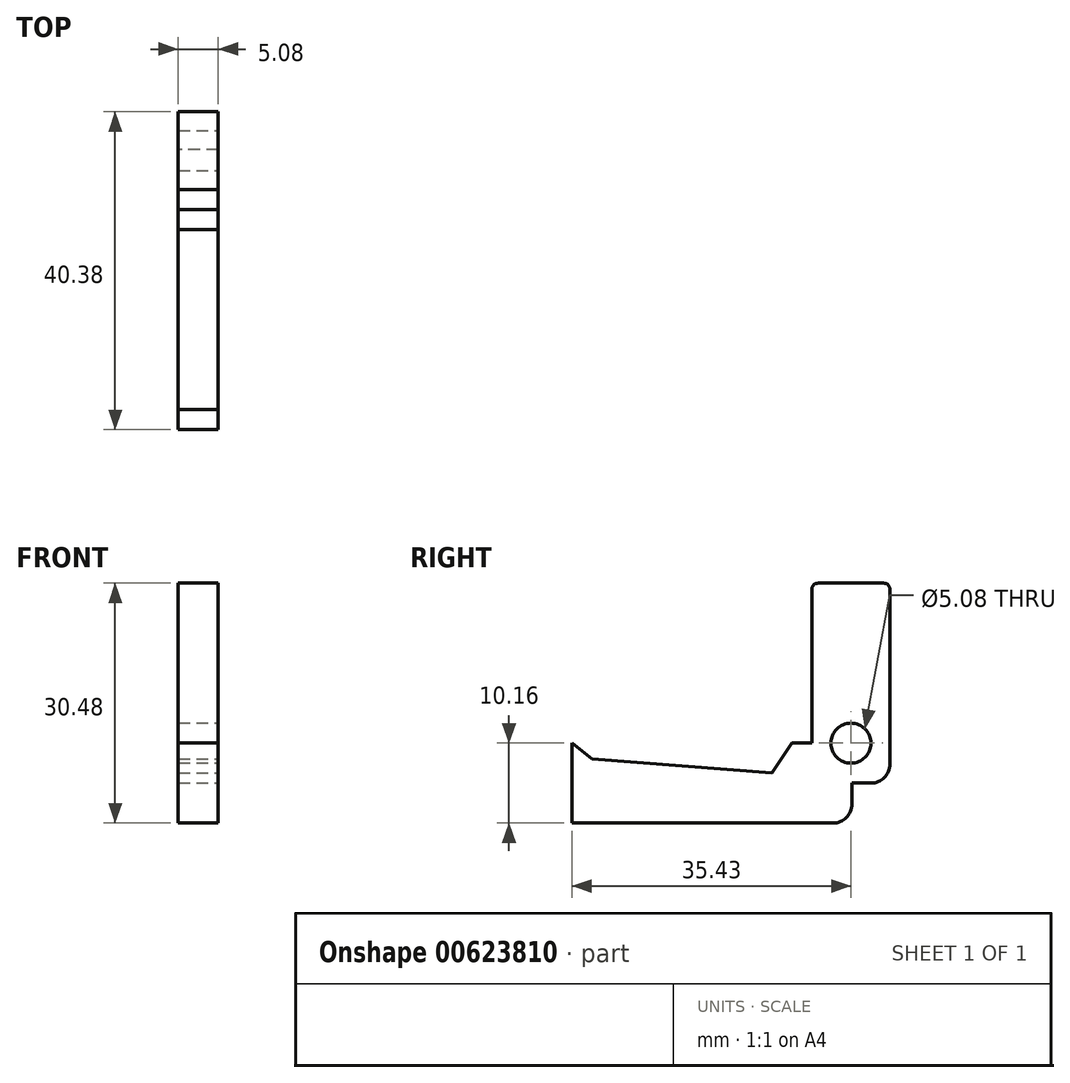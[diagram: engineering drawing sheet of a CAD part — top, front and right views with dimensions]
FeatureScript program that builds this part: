
annotation { "Feature Type Name" : "Feature", "Feature Type Description" : "" }
export const myFeature = defineFeature(function(context is Context, id is Id, definition is map)
    precondition{}
    {
        {
            var Q0;
            Q0=qCreatedBy(makeId("Top.planeOp"),FACE);
            var sketch = newSketch(context, id + "F0", { "sketchPlane" : qUnion([Q0])});
            skLineSegment(sketch, "E0.bottom", {"start": v(-2.54, 4.95) * mm, "end": v(2.54, 4.95) * mm});
            skLineSegment(sketch, "E0.top", {"start": v(-2.54, -4.95) * mm, "end": v(2.54, -4.95) * mm});
            skLineSegment(sketch, "E0.left", {"start": v(-2.54, 4.95) * mm, "end": v(-2.54, -4.95) * mm});
            skLineSegment(sketch, "E0.right", {"start": v(2.54, 4.95) * mm, "end": v(2.54, -4.95) * mm});
            skPoint(sketch, "E0.middle", {"position": v(0, 0) * mm});
            skSolve(sketch);
        }
        {
            var Q0;
            Q0=makeQuery(id+"F0.imprint","IMPRINT",FACE,{"disambiguationData":[TD([[makeQuery(id+"F0.imprint","IMPRINT",EDGE,{"derivedFrom":sQuery(id+"F0.wireOp",EDGE,"E0.bottom")}),-1.0]])]});
            extrude(context, id + "F1", {"entities" : qUnion([Q0]), "depth" : 25.4 * mm, "offsetDistance" : 25.4 * mm});
        }
        {
            var Q0;
            Q0=makeQuery(id+"F1.opExtrude","SWEPT_FACE",FACE,{"disambiguationData":[OSD([sQuery(id+"F0.wireOp",EDGE,"E0.top")])]});
            var sketch = newSketch(context, id + "F2", { "sketchPlane" : qUnion([Q0])});
            skLineSegment(sketch, "E1.bottom", {"start": v(2.54, 0) * mm, "end": v(-2.54, 0) * mm});
            skLineSegment(sketch, "E1.top", {"start": v(2.54, 5.08) * mm, "end": v(-2.54, 5.08) * mm});
            skLineSegment(sketch, "E1.left", {"start": v(2.54, 0) * mm, "end": v(2.54, 5.08) * mm});
            skLineSegment(sketch, "E1.right", {"start": v(-2.54, 0) * mm, "end": v(-2.54, 5.08) * mm});
            skSolve(sketch);
        }
        {
            var Q0;
            Q0=makeQuery(id+"F2.imprint","IMPRINT",FACE,{"disambiguationData":[TD([[makeQuery(id+"F2.imprint","IMPRINT",EDGE,{"derivedFrom":sQuery(id+"F2.wireOp",EDGE,"E1.bottom")}),1.0]])]});
            extrude(context, id + "F3", {"entities" : qUnion([Q0]), "operationType" : NewBodyOperationType.ADD, "depth" : 5.08 * mm, "offsetDistance" : 25.4 * mm});
        }
        {
            var Q0;
            Q0=makeQuery(id+"F3.boolean.opBoolean","MERGE",FACE,{"derivedFrom":[makeQuery(id+"F1.opExtrude","CAP_FACE",FACE,{"disambiguationData":[OSD([sQuery(id+"F0.wireOp",EDGE,"E0.bottom"),sQuery(id+"F0.wireOp",EDGE,"E0.top"),sQuery(id+"F0.wireOp",EDGE,"E0.left"),sQuery(id+"F0.wireOp",EDGE,"E0.right")])],"isStart":true}),makeQuery(id+"F3.opExtrude","SWEPT_FACE",FACE,{"disambiguationData":[OSD([sQuery(id+"F2.wireOp",EDGE,"E1.bottom")])]})]});
            var sketch = newSketch(context, id + "F4", { "sketchPlane" : qUnion([Q0])});
            skLineSegment(sketch, "E2.bottom", {"start": v(2.54, 10.03) * mm, "end": v(-2.54, 10.03) * mm});
            skLineSegment(sketch, "E2.top", {"start": v(2.54, 4.95) * mm, "end": v(-2.54, 4.95) * mm});
            skLineSegment(sketch, "E2.left", {"start": v(2.54, 10.03) * mm, "end": v(2.54, 4.95) * mm});
            skLineSegment(sketch, "E2.right", {"start": v(-2.54, 10.03) * mm, "end": v(-2.54, 4.95) * mm});
            skSolve(sketch);
        }
        {
            var Q0;
            Q0=makeQuery(id+"F4.imprint","IMPRINT",FACE,{"disambiguationData":[TD([[makeQuery(id+"F4.imprint","IMPRINT",EDGE,{"derivedFrom":sQuery(id+"F4.wireOp",EDGE,"E2.bottom")}),-1.0]])]});
            extrude(context, id + "F5", {"entities" : qUnion([Q0]), "operationType" : NewBodyOperationType.ADD, "depth" : 5.08 * mm, "offsetDistance" : 25.4 * mm});
        }
        {
            var Q0;
            Q0=makeQuery(id+"F5.opExtrude","SWEPT_FACE",FACE,{"disambiguationData":[OSD([sQuery(id+"F4.wireOp",EDGE,"E2.top")])]});
            extrude(context, id + "F6", {"entities" : qUnion([Q0]), "operationType" : NewBodyOperationType.ADD, "depth" : 5.08 * mm, "offsetDistance" : 25.4 * mm});
        }
        {
            var Q0;
            Q0=makeQuery(id+"F5.boolean.opBoolean","MERGE",FACE,{"derivedFrom":[makeQuery(id+"F3.opExtrude","CAP_FACE",FACE,{"disambiguationData":[OSD([sQuery(id+"F2.wireOp",EDGE,"E1.bottom"),sQuery(id+"F2.wireOp",EDGE,"E1.top"),sQuery(id+"F2.wireOp",EDGE,"E1.left"),sQuery(id+"F2.wireOp",EDGE,"E1.right")])],"isStart":false}),makeQuery(id+"F5.opExtrude","SWEPT_FACE",FACE,{"disambiguationData":[OSD([sQuery(id+"F4.wireOp",EDGE,"E2.bottom")])]})]});
            extrude(context, id + "F7", {"entities" : qUnion([Q0]), "operationType" : NewBodyOperationType.ADD, "depth" : 25.4 * mm, "offsetDistance" : 25.4 * mm});
        }
        {
            var Q0;
            {var subQ0=sQuery(id+"F4.wireOp",EDGE,"E2.left");var subQ1=sQuery(id+"F2.wireOp",EDGE,"E1.left");var subQ2=sQuery(id+"F0.wireOp",EDGE,"E0.right");Q0=makeQuery(id+"F7.boolean.opBoolean","MERGE",FACE,{"derivedFrom":[makeQuery(id+"F6.boolean.opBoolean","MERGE",FACE,{"derivedFrom":[makeQuery(id+"F5.boolean.opBoolean","MERGE",FACE,{"derivedFrom":[makeQuery(id+"F3.boolean.opBoolean","MERGE",FACE,{"derivedFrom":[makeQuery(id+"F1.opExtrude","SWEPT_FACE",FACE,{"disambiguationData":[OSD([subQ2])]}),makeQuery(id+"F3.opExtrude","SWEPT_FACE",FACE,{"disambiguationData":[OSD([subQ1])]})]}),makeQuery(id+"F5.opExtrude","SWEPT_FACE",FACE,{"disambiguationData":[OSD([subQ0])]})]}),makeQuery(id+"F6.opExtrude","SWEPT_FACE",FACE,{"disambiguationData":[OSD([subQ2,sQuery(id+"F2.wireOp",EDGE,"E1.bottom"),subQ1,sQuery(id+"F4.wireOp",EDGE,"E2.top"),subQ0])]})]}),makeQuery(id+"F7.opExtrude","SWEPT_FACE",FACE,{"disambiguationData":[OSD([subQ1,sQuery(id+"F4.wireOp",EDGE,"E2.bottom"),subQ0])]})]});}
            var sketch = newSketch(context, id + "F8", { "sketchPlane" : qUnion([Q0])});
            skLineSegment(sketch, "E3.bottom", {"start": v(-35.43, 5.08) * mm, "end": v(-10.03, 5.08) * mm});
            skLineSegment(sketch, "E3.top", {"start": v(-35.43, -5.08) * mm, "end": v(-10.03, -5.08) * mm});
            skLineSegment(sketch, "E3.left", {"start": v(-35.43, 5.08) * mm, "end": v(-35.43, -5.08) * mm});
            skLineSegment(sketch, "E3.right", {"start": v(-10.03, 5.08) * mm, "end": v(-10.03, -5.08) * mm});
            skLineSegment(sketch, "E4", {"start": v(-20.2, 5.08) * mm, "end": v(-20.2, -5.08) * mm});
            skLineSegment(sketch, "E5", {"start": v(-20.2, -5.08) * mm, "end": v(-10.03, -5.08) * mm});
            skLineSegment(sketch, "E6", {"start": v(-10.03, -5.08) * mm, "end": v(-20.2, -5.08) * mm});
            skLineSegment(sketch, "E7", {"start": v(-15.11, -5.08) * mm, "end": v(-15.11, 5.08) * mm});
            skLineSegment(sketch, "E8", {"start": v(-10.03, -5.08) * mm, "end": v(-15.11, -5.08) * mm});
            skLineSegment(sketch, "E9", {"start": v(-12.57, -5.08) * mm, "end": v(-12.57, 5.08) * mm});
            skLineSegment(sketch, "E10.MirrorCS", {"start": v(-17.65, -5.08) * mm, "end": v(-17.65, 5.08) * mm});
            skLineSegment(sketch, "E11.MirrorCS", {"start": v(-22.73, -5.08) * mm, "end": v(-22.73, 5.08) * mm});
            skLineSegment(sketch, "E12.MirrorCS", {"start": v(-25.27, -5.08) * mm, "end": v(-25.27, 5.08) * mm});
            skLineSegment(sketch, "E13.MirrorCS", {"start": v(-27.81, -5.08) * mm, "end": v(-27.81, 5.08) * mm});
            skLineSegment(sketch, "E14.MirrorCS", {"start": v(-30.35, 5.08) * mm, "end": v(-30.35, -5.08) * mm});
            skLineSegment(sketch, "E15", {"start": v(-30.35, -5.08) * mm, "end": v(-35.43, -5.08) * mm});
            skLineSegment(sketch, "E16", {"start": v(-32.9, -5.08) * mm, "end": v(-32.9, 5.08) * mm});
            skLineSegment(sketch, "E17", {"start": v(-30.35, 0) * mm, "end": v(-30.35, 5.08) * mm});
            skLineSegment(sketch, "E18", {"start": v(-4.95, 5.08) * mm, "end": v(-10.03, 5.08) * mm});
            skLineSegment(sketch, "E19", {"start": v(-10.03, 1.27) * mm, "end": v(-7.5, 5.08) * mm});
            skLineSegment(sketch, "E20", {"start": v(-10.03, 1.27) * mm, "end": v(-32.9, 3.05) * mm});
            skLineSegment(sketch, "E21", {"start": v(-32.9, 3.05) * mm, "end": v(-35.43, 5.08) * mm});
            skSolve(sketch);
        }
        {
            var Q0;
            {var subQ3=sQuery(id+"F8.wireOp",EDGE,"E19");Q0=makeQuery(id+"F8.imprint","IMPRINT",FACE,{"disambiguationData":[TD([[makeQuery(id+"F8.imprint","IMPRINT",EDGE,{"derivedFrom":subQ3}),1.0]])]});}
            var Q1;
            {var subQ1=sQuery(id+"F8.wireOp",EDGE,"E3.bottom");var subQ3=sQuery(id+"F8.wireOp",EDGE,"E9");var subQ4=makeQuery(id+"F8.imprint","INTERSECT",VERTEX,{"derivedFrom":[subQ1,subQ3]});Q1=makeQuery(id+"F8.imprint","IMPRINT",FACE,{"disambiguationData":[TD([[makeQuery(id+"F8.imprint","IMPRINT",EDGE,{"disambiguationData":[TD([[subQ4,1.0]])],"derivedFrom":subQ3}),-1.0]])]});}
            var Q2;
            {var subQ0=sQuery(id+"F8.wireOp",EDGE,"E7");var subQ1=sQuery(id+"F8.wireOp",EDGE,"E3.bottom");var subQ2=makeQuery(id+"F8.imprint","INTERSECT",VERTEX,{"derivedFrom":[subQ1,subQ0]});Q2=makeQuery(id+"F8.imprint","IMPRINT",FACE,{"disambiguationData":[TD([[makeQuery(id+"F8.imprint","IMPRINT",EDGE,{"disambiguationData":[TD([[subQ2,-1.0]])],"derivedFrom":subQ1}),-1.0]])]});}
            var Q3;
            {var subQ0=sQuery(id+"F8.wireOp",EDGE,"E7");var subQ1=sQuery(id+"F8.wireOp",EDGE,"E3.bottom");var subQ2=makeQuery(id+"F8.imprint","INTERSECT",VERTEX,{"derivedFrom":[subQ1,subQ0]});Q3=makeQuery(id+"F8.imprint","IMPRINT",FACE,{"disambiguationData":[TD([[makeQuery(id+"F8.imprint","IMPRINT",EDGE,{"disambiguationData":[TD([[subQ2,1.0]])],"derivedFrom":subQ1}),-1.0]])]});}
            var Q4;
            {var subQ0=sQuery(id+"F8.wireOp",EDGE,"E4");var subQ1=sQuery(id+"F8.wireOp",EDGE,"E3.bottom");var subQ2=makeQuery(id+"F8.imprint","INTERSECT",VERTEX,{"derivedFrom":[subQ1,subQ0]});Q4=makeQuery(id+"F8.imprint","IMPRINT",FACE,{"disambiguationData":[TD([[makeQuery(id+"F8.imprint","IMPRINT",EDGE,{"disambiguationData":[TD([[subQ2,1.0]])],"derivedFrom":subQ1}),-1.0]])]});}
            var Q5;
            {var subQ0=sQuery(id+"F8.wireOp",EDGE,"E4");var subQ1=sQuery(id+"F8.wireOp",EDGE,"E3.bottom");var subQ2=makeQuery(id+"F8.imprint","INTERSECT",VERTEX,{"derivedFrom":[subQ1,subQ0]});Q5=makeQuery(id+"F8.imprint","IMPRINT",FACE,{"disambiguationData":[TD([[makeQuery(id+"F8.imprint","IMPRINT",EDGE,{"disambiguationData":[TD([[subQ2,-1.0]])],"derivedFrom":subQ1}),-1.0]])]});}
            var Q6;
            {var subQ0=sQuery(id+"F8.wireOp",EDGE,"E11.MirrorCS");var subQ1=sQuery(id+"F8.wireOp",EDGE,"E3.bottom");var subQ2=makeQuery(id+"F8.imprint","INTERSECT",VERTEX,{"derivedFrom":[subQ1,subQ0]});Q6=makeQuery(id+"F8.imprint","IMPRINT",FACE,{"disambiguationData":[TD([[makeQuery(id+"F8.imprint","IMPRINT",EDGE,{"disambiguationData":[TD([[subQ2,1.0]])],"derivedFrom":subQ1}),-1.0]])]});}
            var Q7;
            {var subQ0=sQuery(id+"F8.wireOp",EDGE,"E12.MirrorCS");var subQ1=sQuery(id+"F8.wireOp",EDGE,"E3.bottom");var subQ2=makeQuery(id+"F8.imprint","INTERSECT",VERTEX,{"derivedFrom":[subQ1,subQ0]});Q7=makeQuery(id+"F8.imprint","IMPRINT",FACE,{"disambiguationData":[TD([[makeQuery(id+"F8.imprint","IMPRINT",EDGE,{"disambiguationData":[TD([[subQ2,1.0]])],"derivedFrom":subQ1}),-1.0]])]});}
            var Q8;
            {var subQ0=sQuery(id+"F8.wireOp",EDGE,"E13.MirrorCS");var subQ1=sQuery(id+"F8.wireOp",EDGE,"E3.bottom");var subQ2=makeQuery(id+"F8.imprint","INTERSECT",VERTEX,{"derivedFrom":[subQ1,subQ0]});Q8=makeQuery(id+"F8.imprint","IMPRINT",FACE,{"disambiguationData":[TD([[makeQuery(id+"F8.imprint","IMPRINT",EDGE,{"disambiguationData":[TD([[subQ2,1.0]])],"derivedFrom":subQ1}),-1.0]])]});}
            var Q9;
            {var subQ0=sQuery(id+"F8.wireOp",EDGE,"E16");var subQ1=sQuery(id+"F8.wireOp",EDGE,"E3.bottom");var subQ2=makeQuery(id+"F8.imprint","INTERSECT",VERTEX,{"derivedFrom":[subQ1,subQ0]});Q9=makeQuery(id+"F8.imprint","IMPRINT",FACE,{"disambiguationData":[TD([[makeQuery(id+"F8.imprint","IMPRINT",EDGE,{"disambiguationData":[TD([[subQ2,-1.0]])],"derivedFrom":subQ1}),-1.0]])]});}
            var Q10;
            {var subQ0=sQuery(id+"F8.wireOp",EDGE,"E21");Q10=makeQuery(id+"F8.imprint","IMPRINT",FACE,{"disambiguationData":[TD([[makeQuery(id+"F8.imprint","IMPRINT",EDGE,{"derivedFrom":subQ0}),-1.0]])]});}
            extrude(context, id + "F9", {"entities" : qUnion([Q0, Q1, Q2, Q3, Q4, Q5, Q6, Q7, Q8, Q9, Q10]), "operationType" : NewBodyOperationType.REMOVE, "endBound" : BoundingType.THROUGH_ALL, "oppositeDirection" : true, "depth" : 25.4 * mm, "offsetDistance" : 25.4 * mm});
        }
        {
            var Q0;
            {var subQ0=sQuery(id+"F4.wireOp",EDGE,"E2.top");Q0=makeQuery(id+"F6.opExtrude","CAP_EDGE",EDGE,{"disambiguationData":[OSD([subQ0]),TDD([makeQuery(id+"F5.opExtrude","CAP_EDGE",EDGE,{"disambiguationData":[OSD([subQ0])],"isStart":true})])],"isStart":false});}
            var Q1;
            {var subQ0=sQuery(id+"F4.wireOp",EDGE,"E2.top");Q1=makeQuery(id+"F6.opExtrude","CAP_EDGE",EDGE,{"disambiguationData":[OSD([subQ0]),TDD([makeQuery(id+"F5.opExtrude","CAP_EDGE",EDGE,{"disambiguationData":[OSD([subQ0])],"isStart":false})])],"isStart":false});}
            var Q2;
            Q2=makeQuery(id+"F1.opExtrude","CAP_EDGE",EDGE,{"disambiguationData":[OSD([sQuery(id+"F0.wireOp",EDGE,"E0.bottom")])],"isStart":true});
            fillet(context, id + "F10", {"entities" : qUnion([Q0, Q1, Q2]), "radius" : 2.41 * mm, "tangentPropagation" : true, "allowEdgeOverflow" : false});
        }
        {
            var Q0;
            {var subQ0=sQuery(id+"F4.wireOp",EDGE,"E2.left");var subQ1=sQuery(id+"F2.wireOp",EDGE,"E1.left");var subQ2=sQuery(id+"F0.wireOp",EDGE,"E0.right");Q0=makeQuery(id+"F7.boolean.opBoolean","MERGE",FACE,{"derivedFrom":[makeQuery(id+"F6.boolean.opBoolean","MERGE",FACE,{"derivedFrom":[makeQuery(id+"F5.boolean.opBoolean","MERGE",FACE,{"derivedFrom":[makeQuery(id+"F3.boolean.opBoolean","MERGE",FACE,{"derivedFrom":[makeQuery(id+"F1.opExtrude","SWEPT_FACE",FACE,{"disambiguationData":[OSD([subQ2])]}),makeQuery(id+"F3.opExtrude","SWEPT_FACE",FACE,{"disambiguationData":[OSD([subQ1])]})]}),makeQuery(id+"F5.opExtrude","SWEPT_FACE",FACE,{"disambiguationData":[OSD([subQ0])]})]}),makeQuery(id+"F6.opExtrude","SWEPT_FACE",FACE,{"disambiguationData":[OSD([subQ2,sQuery(id+"F2.wireOp",EDGE,"E1.bottom"),subQ1,sQuery(id+"F4.wireOp",EDGE,"E2.top"),subQ0])]})]}),makeQuery(id+"F7.opExtrude","SWEPT_FACE",FACE,{"disambiguationData":[OSD([subQ1,sQuery(id+"F4.wireOp",EDGE,"E2.bottom"),subQ0])]})]});}
            var sketch = newSketch(context, id + "F11", { "sketchPlane" : qUnion([Q0])});
            skCircle(sketch, "E22", {"center": v(0, 5.08) * mm, "radius": 2.54 * mm});
            skSolve(sketch);
        }
        {
            var Q0;
            Q0=makeQuery(id+"F11.imprint","IMPRINT",FACE,{"disambiguationData":[TD([[makeQuery(id+"F11.imprint","IMPRINT",EDGE,{"derivedFrom":sQuery(id+"F11.wireOp",EDGE,"E22")}),1.0]])]});
            extrude(context, id + "F12", {"entities" : qUnion([Q0]), "operationType" : NewBodyOperationType.REMOVE, "endBound" : BoundingType.THROUGH_ALL, "oppositeDirection" : true, "depth" : 25.4 * mm, "offsetDistance" : 25.4 * mm});
        }
        {
            var Q0;
            Q0=makeQuery(id+"F1.opExtrude","CAP_EDGE",EDGE,{"disambiguationData":[OSD([sQuery(id+"F0.wireOp",EDGE,"E0.bottom")])],"isStart":false});
            var Q1;
            Q1=makeQuery(id+"F1.opExtrude","CAP_EDGE",EDGE,{"disambiguationData":[OSD([sQuery(id+"F0.wireOp",EDGE,"E0.top")])],"isStart":false});
            fillet(context, id + "F13", {"entities" : qUnion([Q0, Q1]), "radius" : 0.76 * mm, "tangentPropagation" : true, "allowEdgeOverflow" : false});
        }
    });
